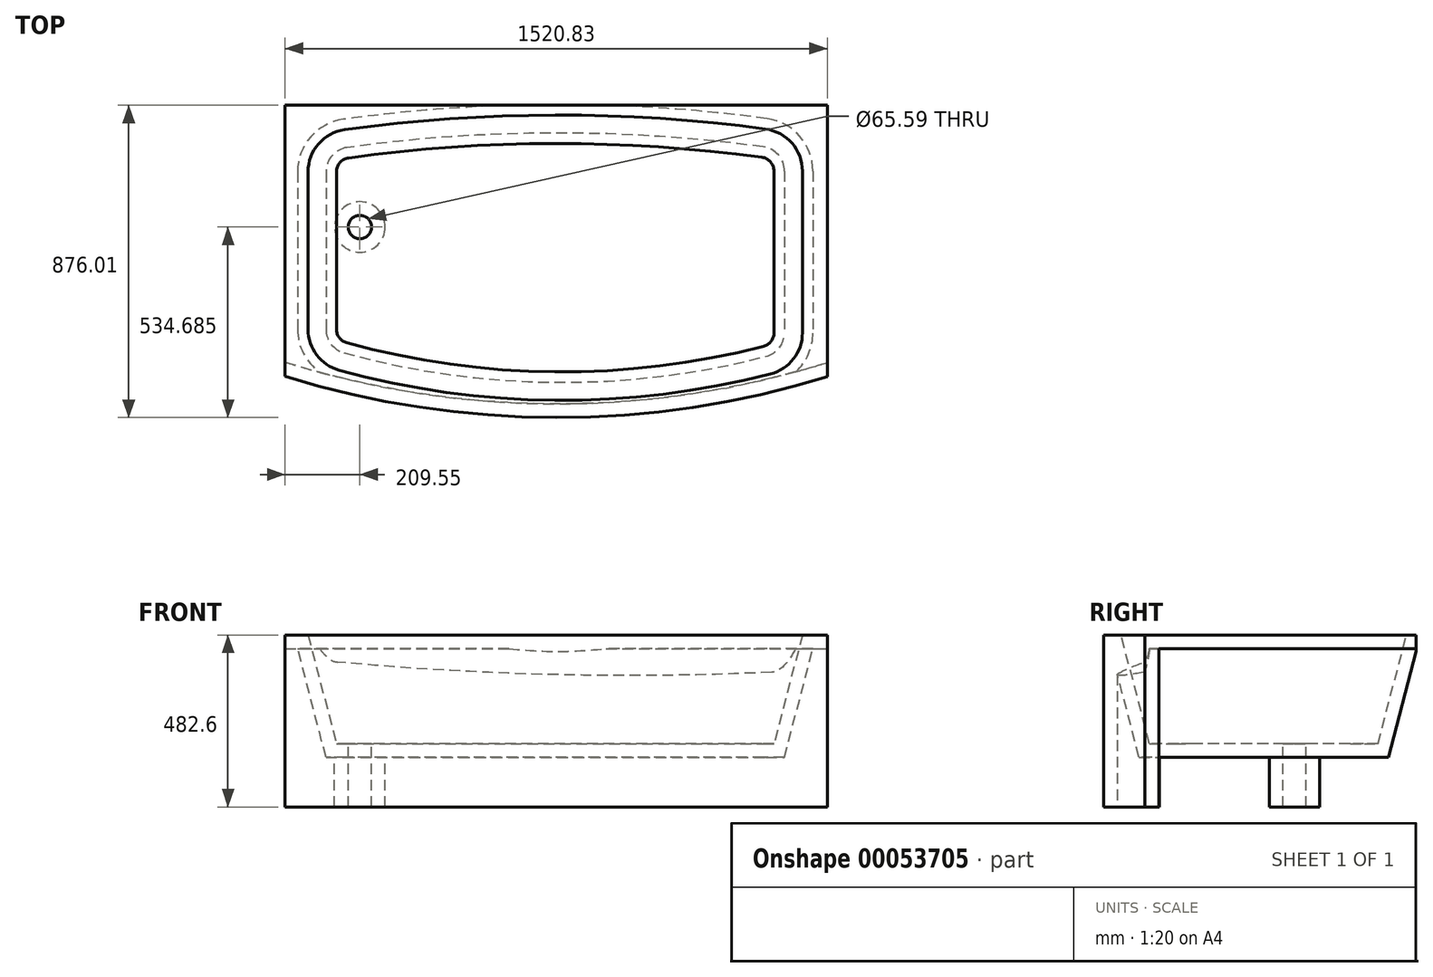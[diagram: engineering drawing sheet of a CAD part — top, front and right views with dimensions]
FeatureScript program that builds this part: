
annotation { "Feature Type Name" : "Feature", "Feature Type Description" : "" }
export const myFeature = defineFeature(function(context is Context, id is Id, definition is map)
    precondition{}
    {
        {
            var Q0;
            Q0=qCreatedBy(makeId("Top.planeOp"),FACE);
            var sketch = newSketch(context, id + "F0", { "sketchPlane" : qUnion([Q0])});
            skLineSegment(sketch, "E0", {"start": v(0, 0) * mm, "end": v(758.83, 0) * mm});
            skLineSegment(sketch, "E1", {"start": v(0, 0) * mm, "end": v(-762, 0) * mm});
            skLineSegment(sketch, "E2", {"start": v(-762, 0) * mm, "end": v(-762, -760.43) * mm});
            skLineSegment(sketch, "E3", {"start": v(0, 0) * mm, "end": v(0, 1772.12) * mm, "construction": true});
            skLineSegment(sketch, "E4", {"start": v(758.83, 0) * mm, "end": v(758.83, -761.4) * mm});
            skArc(sketch, "E5", {"start": v(-762, -760.43) * mm, "mid": v(-1.66, -876) * mm, "end": v(758.83, -761.4) * mm});
            skSolve(sketch);
        }
        {
            var Q0;
            Q0=makeQuery(id+"F0.imprint","IMPRINT",FACE,{"disambiguationData":[TD([[makeQuery(id+"F0.imprint","IMPRINT",EDGE,{"derivedFrom":sQuery(id+"F0.wireOp",EDGE,"E0")}),-1.0]])]});
            extrude(context, id + "F1", {"entities" : qUnion([Q0]), "depth" : 482.6 * mm});
        }
        {
            var Q0;
            Q0=makeQuery(id+"F1.opExtrude","CAP_FACE",FACE,{"disambiguationData":[OSD([sQuery(id+"F0.wireOp",EDGE,"E0"),sQuery(id+"F0.wireOp",EDGE,"E1"),sQuery(id+"F0.wireOp",EDGE,"E2"),sQuery(id+"F0.wireOp",EDGE,"E4"),sQuery(id+"F0.wireOp",EDGE,"E5")])],"isStart":false});
            var sketch = newSketch(context, id + "F2", { "sketchPlane" : qUnion([Q0])});
            skArc(sketch, "E6", {"start": v(585.67, -66.4) * mm, "mid": v(-4.6, -27.3) * mm, "end": v(-594.74, -68.22) * mm});
            skArc(sketch, "E7", {"start": v(-610.19, -743.27) * mm, "mid": v(-6.01, -827.73) * mm, "end": v(599.51, -753.6) * mm});
            skLineSegment(sketch, "E8", {"start": v(-697.71, -186.35) * mm, "end": v(-697.71, -628.32) * mm});
            skLineSegment(sketch, "E9", {"start": v(689, -184.58) * mm, "end": v(689, -638.12) * mm});
            skPoint(sketch, "E10.visualSharp", {"position": v(-697.71, -83.66) * mm});
            skArc(sketch, "E10.filletArc", {"start": v(-594.74, -68.22) * mm, "mid": v(-668.35, -108) * mm, "end": v(-697.71, -186.35) * mm});
            skPoint(sketch, "E11.visualSharp", {"position": v(-697.71, -717.27) * mm});
            skArc(sketch, "E11.filletArc", {"start": v(-697.71, -628.32) * mm, "mid": v(-673.34, -700.56) * mm, "end": v(-610.19, -743.27) * mm});
            skPoint(sketch, "E12.visualSharp", {"position": v(689, -728.64) * mm});
            skArc(sketch, "E12.filletArc", {"start": v(599.51, -753.6) * mm, "mid": v(664.01, -711.17) * mm, "end": v(689, -638.12) * mm});
            skPoint(sketch, "E13.visualSharp", {"position": v(689, -81.57) * mm});
            skArc(sketch, "E13.filletArc", {"start": v(689, -184.58) * mm, "mid": v(659.53, -106.08) * mm, "end": v(585.67, -66.4) * mm});
            skSolve(sketch);
        }
        {
            var Q0;
            Q0=makeQuery(id+"F2.imprint","IMPRINT",FACE,{"disambiguationData":[TD([[makeQuery(id+"F2.imprint","IMPRINT",EDGE,{"derivedFrom":sQuery(id+"F2.wireOp",EDGE,"E6")}),1.0]])]});
            cPlane(context, id + "F3", {"entities" : qUnion([Q0]), "cplaneType" : CPlaneType.OFFSET, "offset" : 304.8 * mm, "oppositeDirection" : true, "width" : 152.4 * mm, "height" : 152.4 * mm});
        }
        {
            var Q0;
            Q0=qCreatedBy(id+"F3.planeOp",FACE);
            var sketch = newSketch(context, id + "F4", { "sketchPlane" : qUnion([Q0])});
            skArc(sketch, "E14.0", {"start": v(609.12, -184.58) * mm, "mid": v(599.4, -158.67) * mm, "end": v(575.01, -145.57) * mm});
            skLineSegment(sketch, "E14.1", {"start": v(609.12, -184.58) * mm, "end": v(609.12, -638.12) * mm});
            skArc(sketch, "E14.2", {"start": v(575.01, -145.57) * mm, "mid": v(-4.47, -107.2) * mm, "end": v(-583.84, -147.36) * mm});
            skArc(sketch, "E14.3", {"start": v(579.58, -676.24) * mm, "mid": v(600.87, -662.24) * mm, "end": v(609.12, -638.12) * mm});
            skArc(sketch, "E14.4", {"start": v(-583.84, -147.36) * mm, "mid": v(-608.14, -160.49) * mm, "end": v(-617.83, -186.35) * mm});
            skLineSegment(sketch, "E14.5", {"start": v(-617.83, -186.35) * mm, "end": v(-617.83, -628.32) * mm});
            skArc(sketch, "E14.6", {"start": v(-617.83, -628.32) * mm, "mid": v(-609.78, -652.16) * mm, "end": v(-588.94, -666.26) * mm});
            skArc(sketch, "E14.7", {"start": v(-588.94, -666.26) * mm, "mid": v(-5.33, -747.85) * mm, "end": v(579.58, -676.24) * mm});
            skSolve(sketch);
        }
        {
            var Q1;
            Q1=makeQuery(id+"F2.imprint","IMPRINT",FACE,{"disambiguationData":[TD([[makeQuery(id+"F2.imprint","IMPRINT",EDGE,{"derivedFrom":sQuery(id+"F2.wireOp",EDGE,"E6")}),1.0]])]});
            var Q2;
            Q2 = qSketchRegion(id + "F4", true);
            loft(context, id + "F5", {"operationType" : NewBodyOperationType.REMOVE, "sheetProfilesArray" : [{ "sheetProfileEntities" : qUnion([Q1]) }, { "sheetProfileEntities" : qUnion([Q2]) }]});
        }
        {
            var Q0;
            Q0=makeQuery(id+"F5.boolean.opBoolean","COPY",FACE,{"derivedFrom":makeQuery(id+"F5.opLoft","CAP_FACE",FACE,{"disambiguationData":[OSD([makeQuery(id+"F4.imprint","IMPRINT",FACE,{"disambiguationData":[TD([[makeQuery(id+"F4.imprint","IMPRINT",EDGE,{"derivedFrom":sQuery(id+"F4.wireOp",EDGE,"E14.0")}),1.0]])]})])],"isStart":true})});
            var sketch = newSketch(context, id + "F6", { "sketchPlane" : qUnion([Q0])});
            skCircle(sketch, "E15", {"center": v(-552.45, -341.33) * mm, "radius": 32.8 * mm});
            skSolve(sketch);
        }
        {
            var Q0;
            Q0 = qSketchRegion(id + "F6", true);
            extrude(context, id + "F7", {"entities" : qUnion([Q0]), "operationType" : NewBodyOperationType.REMOVE, "endBound" : BoundingType.THROUGH_ALL, "oppositeDirection" : true, "depth" : 25.4 * mm});
        }
        {
            var Q0;
            Q0=makeQuery(id+"F1.opExtrude","SWEPT_FACE",FACE,{"disambiguationData":[OSD([sQuery(id+"F0.wireOp",EDGE,"E2")])]});
            var Q1;
            Q1=makeQuery(id+"F1.opExtrude","SWEPT_FACE",FACE,{"disambiguationData":[OSD([sQuery(id+"F0.wireOp",EDGE,"E0"),sQuery(id+"F0.wireOp",EDGE,"E1")])]});
            var Q2;
            Q2=makeQuery(id+"F1.opExtrude","SWEPT_FACE",FACE,{"disambiguationData":[OSD([sQuery(id+"F0.wireOp",EDGE,"E4")])]});
            var Q3;
            Q3=makeQuery(id+"F1.opExtrude","CAP_FACE",FACE,{"disambiguationData":[OSD([sQuery(id+"F0.wireOp",EDGE,"E0"),sQuery(id+"F0.wireOp",EDGE,"E1"),sQuery(id+"F0.wireOp",EDGE,"E2"),sQuery(id+"F0.wireOp",EDGE,"E4"),sQuery(id+"F0.wireOp",EDGE,"E5")])],"isStart":true});
            shell(context, id + "F8", {"entities" : qUnion([Q0, Q1, Q2, Q3]), "thickness" : 38.1 * mm});
        }
    });
